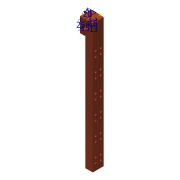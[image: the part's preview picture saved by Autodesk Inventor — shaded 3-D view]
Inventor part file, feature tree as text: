
AUTODESK INVENTOR PART (.ipt)
format: ipt  version: 2016 SP2 (Build 200236200, 236)  size: 154,624 bytes
history: native  units: mm
features: extrude x4, sketch x4, pattern_linear x1, reference x1
ambient origin geometry x8: Origin, YZ Plane, XZ Plane, XY Plane, X Axis, Y Axis, Z Axis, Center Point
bodies: Solid4 (feature_tree)
feature tree (10):
  extrude  "Extrusion3"  Depth=20.0mm
  extrude  "Extrusion4"  Depth=10.0mm TaperAngle=0.0deg
  pattern_linear  "Rectangular Pattern1"  Count1=6  [1 undecoded]
  sketch  "Sketch4"  dims[d20=15.0mm d21=2.0mm d22=1.0mm]
  extrude  "Extrusion5"  Depth=2.0mm
  extrude  "Extrusion6"  Depth=40.0mm
  sketch  "Sketch5"  dims[d23=13.0mm d24=40.0mm d25=20.0mm d26=10.0mm d27=0.0mm d28=0.0mm d29=0.0mm d30=15.0mm d31=25.0mm]
  sketch  "Sketch1"  dims[d4=30.0mm d5=20.0mm]
  sketch  "Sketch3"  dims[d6=350.0mm d7=0.0mm d15=10.0mm d16=0.0mm d17=60.0mm d19=50.0mm]
  reference  "Reference1"
note: 1 required parameter value undecoded (feature->parameter linkage not recoverable at this tier; creation-order binding heuristic only, values carry confidence <= 0.55)
